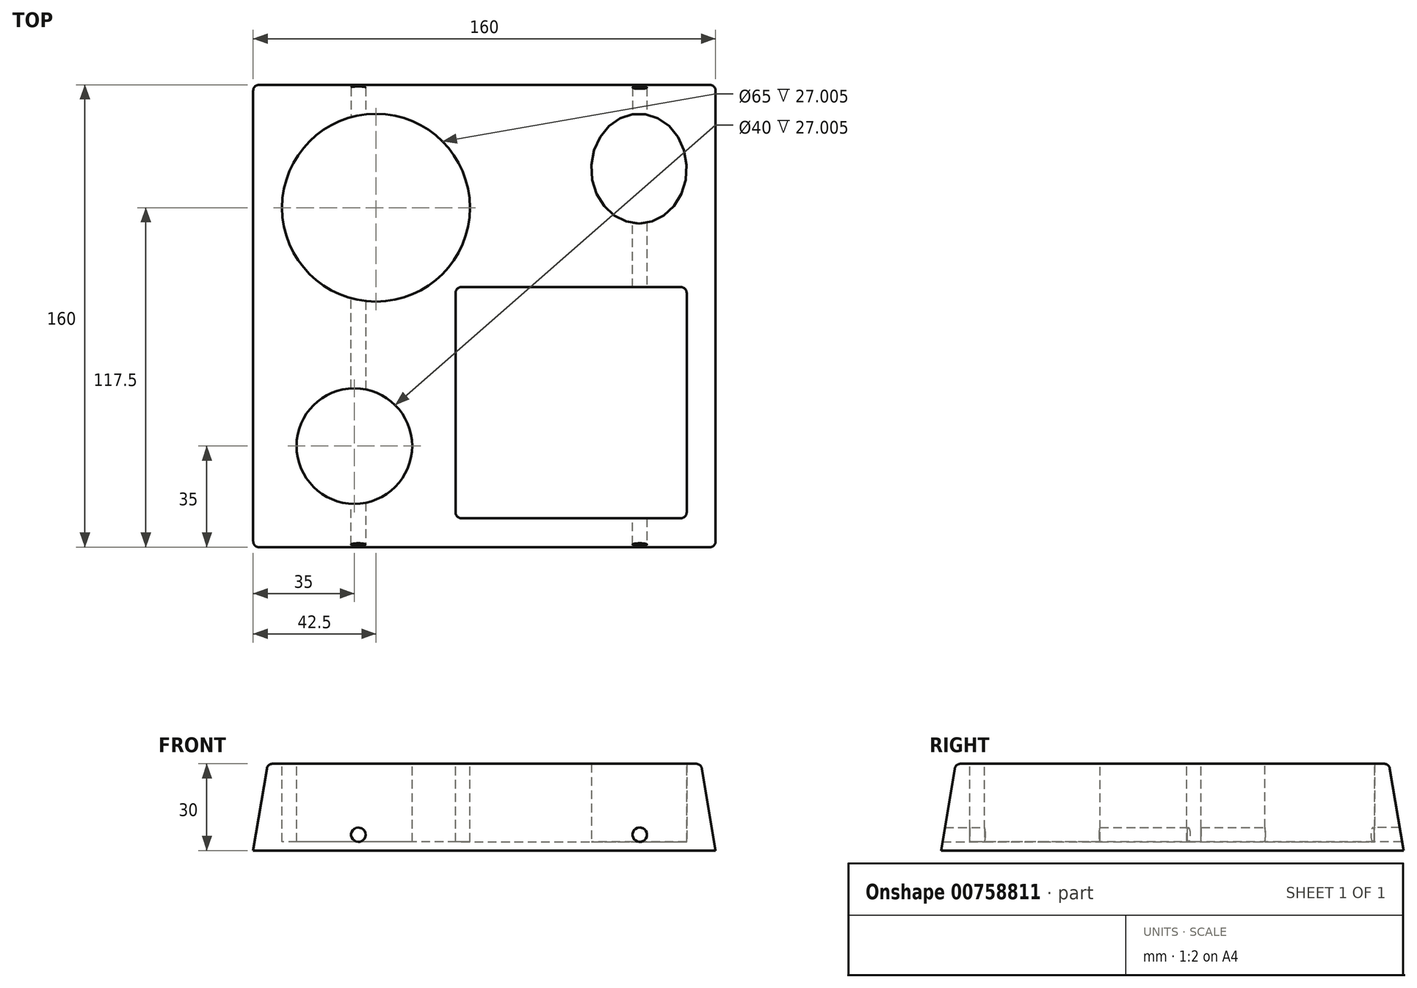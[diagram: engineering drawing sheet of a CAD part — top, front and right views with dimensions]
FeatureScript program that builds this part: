
annotation { "Feature Type Name" : "Feature", "Feature Type Description" : "" }
export const myFeature = defineFeature(function(context is Context, id is Id, definition is map)
    precondition{}
    {
        {
            var Q0;
            Q0=qCreatedBy(makeId("Top.planeOp"),FACE);
            var sketch = newSketch(context, id + "F0", { "sketchPlane" : qUnion([Q0])});
            skLineSegment(sketch, "E0.bottom", {"start": v(0, 0) * mm, "end": v(160, 0) * mm});
            skLineSegment(sketch, "E0.top", {"start": v(0, 160) * mm, "end": v(160, 160) * mm});
            skLineSegment(sketch, "E0.left", {"start": v(0, 0) * mm, "end": v(0, 160) * mm});
            skLineSegment(sketch, "E0.right", {"start": v(160, 0) * mm, "end": v(160, 160) * mm});
            skSolve(sketch);
        }
        {
            var Q0;
            Q0=qCreatedBy(makeId("Top.planeOp"),FACE);
            cPlane(context, id + "F1", {"entities" : qUnion([Q0]), "cplaneType" : CPlaneType.OFFSET, "offset" : 30 * mm, "width" : 150 * mm, "height" : 150 * mm});
        }
        {
            var Q0;
            Q0=qCreatedBy(id+"F1.planeOp",FACE);
            var sketch = newSketch(context, id + "F2", { "sketchPlane" : qUnion([Q0])});
            skLineSegment(sketch, "E1.0.0", {"start": v(160, 160) * mm, "end": v(0, 160) * mm});
            skLineSegment(sketch, "E1.0.1", {"start": v(0, 160) * mm, "end": v(0, 0) * mm});
            skLineSegment(sketch, "E1.0.2", {"start": v(0, 0) * mm, "end": v(160, 0) * mm});
            skLineSegment(sketch, "E1.0.3", {"start": v(160, 0) * mm, "end": v(160, 160) * mm});
            skLineSegment(sketch, "E2.0", {"start": v(155, 155) * mm, "end": v(5, 155) * mm});
            skLineSegment(sketch, "E2.1", {"start": v(155, 5) * mm, "end": v(155, 155) * mm});
            skLineSegment(sketch, "E2.2", {"start": v(5, 5) * mm, "end": v(155, 5) * mm});
            skLineSegment(sketch, "E2.3", {"start": v(5, 155) * mm, "end": v(5, 5) * mm});
            skSolve(sketch);
        }
        {
            var Q0;
            Q0=makeQuery(id+"F2.imprint","IMPRINT",FACE,{"disambiguationData":[TD([[makeQuery(id+"F2.imprint","IMPRINT",EDGE,{"derivedFrom":sQuery(id+"F2.wireOp",EDGE,"E2.0")}),1.0]])]});
            var Q1;
            Q1=makeQuery(id+"F0.imprint","IMPRINT",FACE,{"disambiguationData":[TD([[makeQuery(id+"F0.imprint","IMPRINT",EDGE,{"derivedFrom":sQuery(id+"F0.wireOp",EDGE,"E0.bottom")}),1.0]])]});
            loft(context, id + "F3", {"sheetProfilesArray" : [{ "sheetProfileEntities" : qUnion([Q0]) }, { "sheetProfileEntities" : qUnion([Q1]) }]});
        }
        {
            var Q0;
            Q0=makeQuery(id+"F3.opLoft","CAP_FACE",FACE,{"disambiguationData":[OSD([makeQuery(id+"F2.imprint","IMPRINT",FACE,{"disambiguationData":[TD([[makeQuery(id+"F2.imprint","IMPRINT",EDGE,{"derivedFrom":sQuery(id+"F2.wireOp",EDGE,"E2.0")}),1.0]])]})])],"isStart":true});
            var sketch = newSketch(context, id + "F4", { "sketchPlane" : qUnion([Q0])});
            skEllipse(sketch, "E3", {"center": v(133.5, 131) * mm, "majorRadius": 19 * mm, "minorRadius": 16.5 * mm, "majorAxis": v(0, -1)});
            skCircle(sketch, "E4", {"center": v(42.5, 117.5) * mm, "radius": 32.5 * mm});
            skCircle(sketch, "E5", {"center": v(35, 35) * mm, "radius": 20 * mm});
            skPoint(sketch, "E6", {"position": v(133.5, 150) * mm});
            skPoint(sketch, "E7", {"position": v(133.5, 112) * mm});
            skPoint(sketch, "E8", {"position": v(150, 131) * mm});
            skPoint(sketch, "E9", {"position": v(117, 131) * mm});
            skLineSegment(sketch, "E10.bottom", {"start": v(70, 90) * mm, "end": v(150, 90) * mm});
            skLineSegment(sketch, "E10.top", {"start": v(70, 10) * mm, "end": v(150, 10) * mm});
            skLineSegment(sketch, "E10.left", {"start": v(70, 90) * mm, "end": v(70, 10) * mm});
            skLineSegment(sketch, "E10.right", {"start": v(150, 90) * mm, "end": v(150, 10) * mm});
            skSolve(sketch);
        }
        {
            var Q0;
            Q0=makeQuery(id+"F4.imprint","IMPRINT",FACE,{"disambiguationData":[TD([[makeQuery(id+"F4.imprint","IMPRINT",EDGE,{"derivedFrom":sQuery(id+"F4.wireOp",EDGE,"E4")}),1.0]])]});
            var Q1;
            Q1=makeQuery(id+"F4.imprint","IMPRINT",FACE,{"disambiguationData":[TD([[makeQuery(id+"F4.imprint","IMPRINT",EDGE,{"derivedFrom":sQuery(id+"F4.wireOp",EDGE,"E5")}),1.0]])]});
            var Q2;
            Q2=makeQuery(id+"F4.imprint","IMPRINT",FACE,{"disambiguationData":[TD([[makeQuery(id+"F4.imprint","IMPRINT",EDGE,{"derivedFrom":sQuery(id+"F4.wireOp",EDGE,"E10.bottom")}),-1.0]])]});
            var Q3;
            Q3=makeQuery(id+"F4.imprint","IMPRINT",FACE,{"disambiguationData":[TD([[makeQuery(id+"F4.imprint","IMPRINT",EDGE,{"derivedFrom":sQuery(id+"F4.wireOp",EDGE,"E3")}),1.0]])]});
            extrude(context, id + "F5", {"entities" : qUnion([Q0, Q1, Q2, Q3]), "operationType" : NewBodyOperationType.REMOVE, "oppositeDirection" : true, "depth" : 27 * mm, "offsetDistance" : 25 * mm});
        }
        {
            var Q0;
            Q0=makeQuery(id+"F3.opLoft","SWEPT_FACE",FACE,{"disambiguationData":[OSD([sQuery(id+"F0.wireOp",EDGE,"E0.bottom"),sQuery(id+"F0.wireOp",EDGE,"E0.left"),sQuery(id+"F0.wireOp",EDGE,"E0.right"),sQuery(id+"F2.wireOp",EDGE,"E2.1"),sQuery(id+"F2.wireOp",EDGE,"E2.2"),sQuery(id+"F2.wireOp",EDGE,"E2.3")])]});
            var sketch = newSketch(context, id + "F6", { "sketchPlane" : qUnion([Q0])});
            skCircle(sketch, "E11", {"center": v(133.75, 5.54) * mm, "radius": 2.5 * mm});
            skCircle(sketch, "E12", {"center": v(36.38, 5.55) * mm, "radius": 2.5 * mm});
            skSolve(sketch);
        }
        {
            var Q0;
            Q0=qCreatedBy(makeId("Front.planeOp"),FACE);
            var sketch = newSketch(context, id + "F7", { "sketchPlane" : qUnion([Q0])});
            skEllipse(sketch, "E13.0.0", {"center": v(133.75, 5.47) * mm, "majorRadius": 2.5 * mm, "minorRadius": 2.47 * mm, "majorAxis": v(1, 0)});
            skEllipse(sketch, "E14.0.0", {"center": v(36.38, 5.47) * mm, "majorRadius": 2.5 * mm, "minorRadius": 2.47 * mm, "majorAxis": v(1, 0)});
            skSolve(sketch);
        }
        {
            var Q0;
            Q0=makeQuery(id+"F7.imprint","IMPRINT",FACE,{"disambiguationData":[TD([[makeQuery(id+"F7.imprint","IMPRINT",EDGE,{"derivedFrom":sQuery(id+"F7.wireOp",EDGE,"E13.0.0")}),1.0]])]});
            var Q1;
            Q1=makeQuery(id+"F7.imprint","IMPRINT",FACE,{"disambiguationData":[TD([[makeQuery(id+"F7.imprint","IMPRINT",EDGE,{"derivedFrom":sQuery(id+"F7.wireOp",EDGE,"E14.0.0")}),1.0]])]});
            extrude(context, id + "F8", {"entities" : qUnion([Q0, Q1]), "operationType" : NewBodyOperationType.REMOVE, "endBound" : BoundingType.THROUGH_ALL, "oppositeDirection" : true, "depth" : 25 * mm, "offsetDistance" : 25 * mm});
        }
        {
            var Q0;
            Q0=makeQuery(id+"F3.opLoft","SWEPT_EDGE",EDGE,{"disambiguationData":[OSD([sQuery(id+"F0.wireOp",EDGE,"E0.bottom"),sQuery(id+"F0.wireOp",EDGE,"E0.left"),sQuery(id+"F2.wireOp",EDGE,"E2.2"),sQuery(id+"F2.wireOp",EDGE,"E2.3")])]});
            var Q1;
            Q1=makeQuery(id+"F3.opLoft","SWEPT_EDGE",EDGE,{"disambiguationData":[OSD([sQuery(id+"F0.wireOp",EDGE,"E0.top"),sQuery(id+"F0.wireOp",EDGE,"E0.left"),sQuery(id+"F2.wireOp",EDGE,"E2.0"),sQuery(id+"F2.wireOp",EDGE,"E2.3")])]});
            var Q2;
            Q2=makeQuery(id+"F3.opLoft","SWEPT_EDGE",EDGE,{"disambiguationData":[OSD([sQuery(id+"F0.wireOp",EDGE,"E0.top"),sQuery(id+"F0.wireOp",EDGE,"E0.right"),sQuery(id+"F2.wireOp",EDGE,"E2.0"),sQuery(id+"F2.wireOp",EDGE,"E2.1")])]});
            var Q3;
            Q3=makeQuery(id+"F3.opLoft","SWEPT_EDGE",EDGE,{"disambiguationData":[OSD([sQuery(id+"F0.wireOp",EDGE,"E0.bottom"),sQuery(id+"F0.wireOp",EDGE,"E0.right"),sQuery(id+"F2.wireOp",EDGE,"E2.1"),sQuery(id+"F2.wireOp",EDGE,"E2.2")])]});
            fillet(context, id + "F9", {"entities" : qUnion([Q0, Q1, Q2, Q3]), "radius" : 2 * mm, "tangentPropagation" : true, "allowEdgeOverflow" : false});
        }
        {
            var Q0;
            Q0=makeQuery(id+"F5.boolean.opBoolean","COPY",EDGE,{"derivedFrom":makeQuery(id+"F5.opExtrude","CAP_EDGE",EDGE,{"disambiguationData":[OSD([sQuery(id+"F4.wireOp",EDGE,"E10.right")])],"isStart":true})});
            var Q1;
            Q1=makeQuery(id+"F5.boolean.opBoolean","COPY",EDGE,{"derivedFrom":makeQuery(id+"F5.opExtrude","CAP_EDGE",EDGE,{"disambiguationData":[OSD([sQuery(id+"F4.wireOp",EDGE,"E10.bottom")])],"isStart":true})});
            var Q2;
            Q2=makeQuery(id+"F5.boolean.opBoolean","COPY",EDGE,{"derivedFrom":makeQuery(id+"F5.opExtrude","SWEPT_EDGE",EDGE,{"disambiguationData":[OSD([sQuery(id+"F4.wireOp",EDGE,"E10.bottom"),sQuery(id+"F4.wireOp",EDGE,"E10.right")])]})});
            var Q3;
            Q3=makeQuery(id+"F5.boolean.opBoolean","COPY",EDGE,{"derivedFrom":makeQuery(id+"F5.opExtrude","SWEPT_EDGE",EDGE,{"disambiguationData":[OSD([sQuery(id+"F4.wireOp",EDGE,"E10.top"),sQuery(id+"F4.wireOp",EDGE,"E10.right")])]})});
            var Q4;
            Q4=makeQuery(id+"F5.boolean.opBoolean","COPY",EDGE,{"derivedFrom":makeQuery(id+"F5.opExtrude","SWEPT_EDGE",EDGE,{"disambiguationData":[OSD([sQuery(id+"F4.wireOp",EDGE,"E10.top"),sQuery(id+"F4.wireOp",EDGE,"E10.left")])]})});
            var Q5;
            Q5=makeQuery(id+"F5.boolean.opBoolean","COPY",EDGE,{"derivedFrom":makeQuery(id+"F5.opExtrude","SWEPT_EDGE",EDGE,{"disambiguationData":[OSD([sQuery(id+"F4.wireOp",EDGE,"E10.bottom"),sQuery(id+"F4.wireOp",EDGE,"E10.left")])]})});
            var Q6;
            Q6=makeQuery(id+"F5.boolean.opBoolean","COPY",EDGE,{"derivedFrom":makeQuery(id+"F5.opExtrude","CAP_EDGE",EDGE,{"disambiguationData":[OSD([sQuery(id+"F4.wireOp",EDGE,"E5")])],"isStart":true})});
            var Q7;
            Q7=makeQuery(id+"F5.boolean.opBoolean","COPY",EDGE,{"derivedFrom":makeQuery(id+"F5.opExtrude","CAP_EDGE",EDGE,{"disambiguationData":[OSD([sQuery(id+"F4.wireOp",EDGE,"E4")])],"isStart":true})});
            var Q8;
            Q8=makeQuery(id+"F5.boolean.opBoolean","COPY",EDGE,{"derivedFrom":makeQuery(id+"F5.opExtrude","CAP_EDGE",EDGE,{"disambiguationData":[OSD([sQuery(id+"F4.wireOp",EDGE,"E3")])],"isStart":true})});
            var Q9;
            Q9=makeQuery(id+"F3.opLoft","MID_CAP_EDGE",EDGE,{"disambiguationData":[OSD([sQuery(id+"F2.wireOp",EDGE,"E2.0"),sQuery(id+"F2.wireOp",EDGE,"E2.1"),sQuery(id+"F2.wireOp",EDGE,"E2.3")])],"capPos":0.0});
            fillet(context, id + "F10", {"entities" : qUnion([Q0, Q1, Q2, Q3, Q4, Q5, Q6, Q7, Q8, Q9]), "radius" : 2 * mm, "tangentPropagation" : true, "allowEdgeOverflow" : false});
        }
    });
